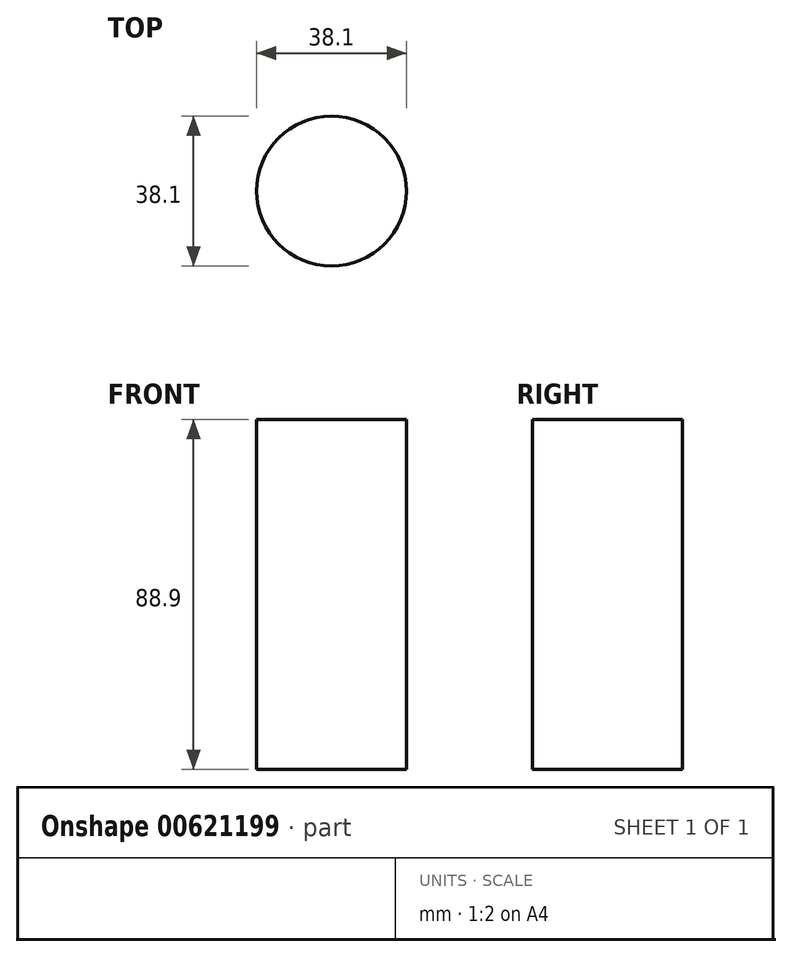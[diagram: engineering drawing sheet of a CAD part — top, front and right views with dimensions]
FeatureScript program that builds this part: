
annotation { "Feature Type Name" : "Feature", "Feature Type Description" : "" }
export const myFeature = defineFeature(function(context is Context, id is Id, definition is map)
    precondition{}
    {
        {
            var Q0;
            Q0=qCreatedBy(makeId("Top.planeOp"),FACE);
            var sketch = newSketch(context, id + "F0", { "sketchPlane" : qUnion([Q0])});
            skCircle(sketch, "E0", {"center": v(0, 0) * mm, "radius": 19.05 * mm});
            skSolve(sketch);
        }
        {
            var Q0;
            Q0=makeQuery(id+"F0.imprint","IMPRINT",FACE,{"disambiguationData":[TD([[makeQuery(id+"F0.imprint","IMPRINT",EDGE,{"derivedFrom":sQuery(id+"F0.wireOp",EDGE,"E0")}),1.0]])]});
            extrude(context, id + "F1", {"entities" : qUnion([Q0]), "depth" : 88.9 * mm, "offsetDistance" : 25.4 * mm});
        }
    });
